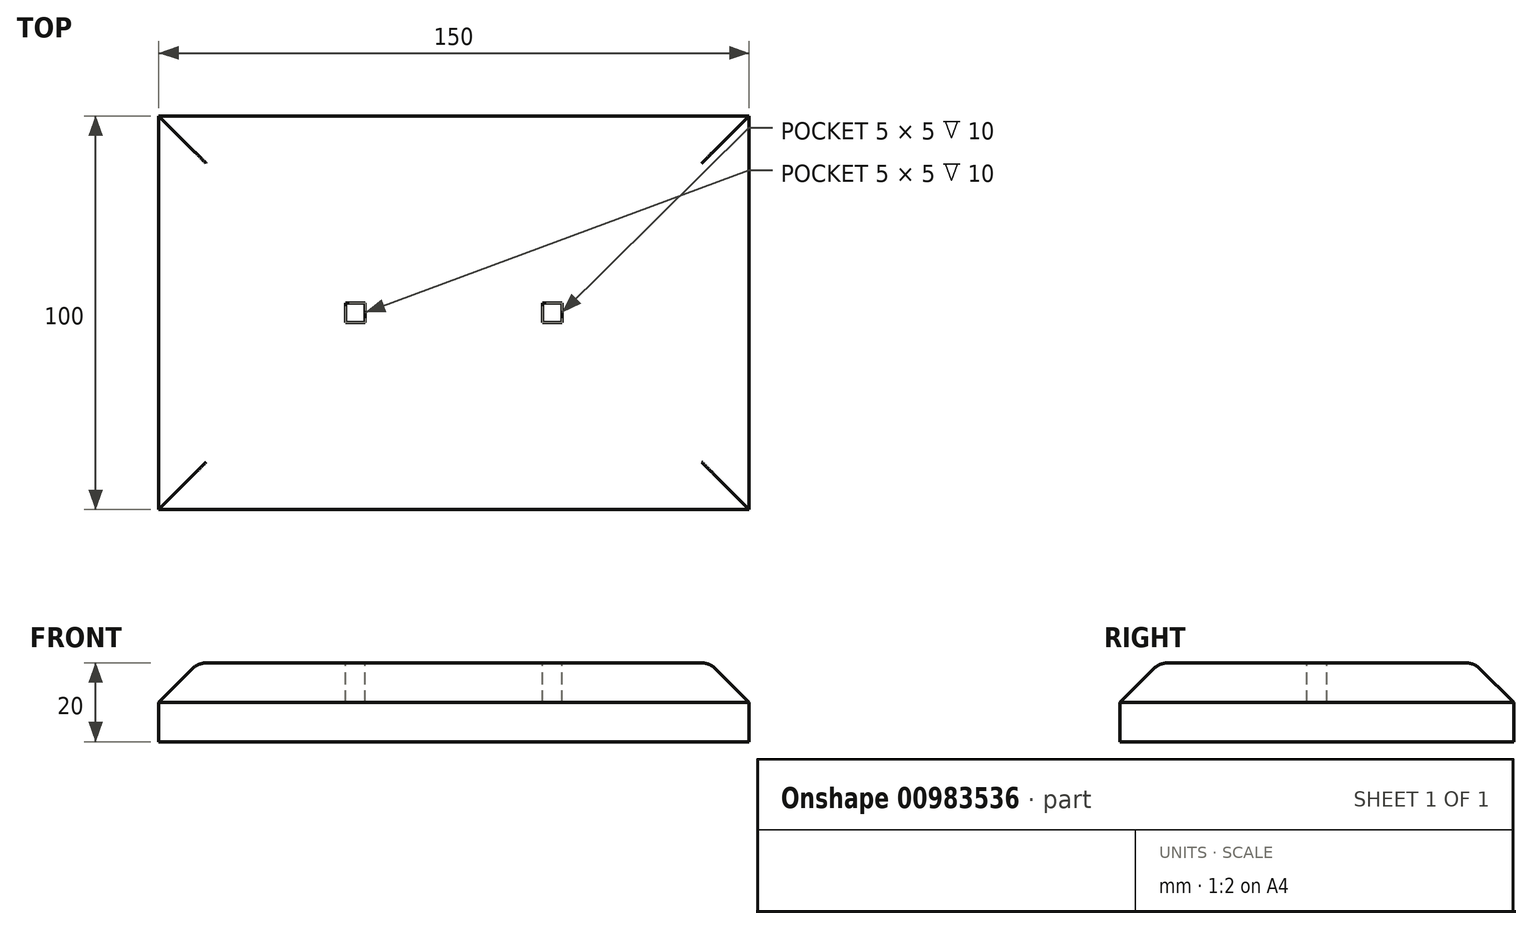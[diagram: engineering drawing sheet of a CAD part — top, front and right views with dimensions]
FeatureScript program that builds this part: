
annotation { "Feature Type Name" : "Feature", "Feature Type Description" : "" }
export const myFeature = defineFeature(function(context is Context, id is Id, definition is map)
    precondition{}
    {
        {
            var Q0;
            Q0=qCreatedBy(makeId("Top.planeOp"),FACE);
            var sketch = newSketch(context, id + "F0", { "sketchPlane" : qUnion([Q0])});
            skLineSegment(sketch, "E0.bottom", {"start": v(-65.87, 0) * mm, "end": v(84.13, 0) * mm});
            skLineSegment(sketch, "E0.top", {"start": v(-65.87, -100) * mm, "end": v(84.13, -100) * mm});
            skLineSegment(sketch, "E0.left", {"start": v(-65.87, 0) * mm, "end": v(-65.87, -100) * mm});
            skLineSegment(sketch, "E0.right", {"start": v(84.13, 0) * mm, "end": v(84.13, -100) * mm});
            skSolve(sketch);
        }
        {
            var Q0;
            Q0 = qSketchRegion(id + "F0", true);
            extrude(context, id + "F1", {"entities" : qUnion([Q0]), "depth" : 20 * mm, "offsetDistance" : 25 * mm});
        }
        {
            var Q0;
            Q0=makeQuery(id+"F1.opExtrude","CAP_EDGE",EDGE,{"disambiguationData":[OSD([sQuery(id+"F0.wireOp",EDGE,"E0.top")])],"isStart":false});
            var Q1;
            Q1=makeQuery(id+"F1.opExtrude","CAP_EDGE",EDGE,{"disambiguationData":[OSD([sQuery(id+"F0.wireOp",EDGE,"E0.left")])],"isStart":false});
            var Q2;
            Q2=makeQuery(id+"F1.opExtrude","CAP_EDGE",EDGE,{"disambiguationData":[OSD([sQuery(id+"F0.wireOp",EDGE,"E0.bottom")])],"isStart":false});
            var Q3;
            Q3=makeQuery(id+"F1.opExtrude","CAP_EDGE",EDGE,{"disambiguationData":[OSD([sQuery(id+"F0.wireOp",EDGE,"E0.right")])],"isStart":false});
            chamfer(context, id + "F2", {"entities" : qUnion([Q0, Q1, Q2, Q3]), "width" : 10 * mm, "tangentPropagation" : true});
        }
        {
            var Q0;
            Q0=makeQuery(id+"F1.opExtrude","CAP_FACE",FACE,{"disambiguationData":[OSD([sQuery(id+"F0.wireOp",EDGE,"E0.bottom"),sQuery(id+"F0.wireOp",EDGE,"E0.top"),sQuery(id+"F0.wireOp",EDGE,"E0.left"),sQuery(id+"F0.wireOp",EDGE,"E0.right")])],"isStart":false});
            var sketch = newSketch(context, id + "F3", { "sketchPlane" : qUnion([Q0])});
            skLineSegment(sketch, "E1", {"start": v(-55.87, -50) * mm, "end": v(74.13, -50) * mm});
            skLineSegment(sketch, "E2", {"start": v(9.13, -90) * mm, "end": v(9.13, -10) * mm});
            skLineSegment(sketch, "E3", {"start": v(9.13, -50) * mm, "end": v(34.13, -50) * mm});
            skLineSegment(sketch, "E4", {"start": v(34.13, -50) * mm, "end": v(34.13, -47.5) * mm});
            skLineSegment(sketch, "E5", {"start": v(31.63, -47.5) * mm, "end": v(34.13, -47.5) * mm});
            skLineSegment(sketch, "E6", {"start": v(31.63, -47.5) * mm, "end": v(31.63, -52.5) * mm});
            skLineSegment(sketch, "E7", {"start": v(31.63, -52.5) * mm, "end": v(36.63, -52.5) * mm});
            skLineSegment(sketch, "E8", {"start": v(36.63, -47.5) * mm, "end": v(36.63, -52.5) * mm});
            skLineSegment(sketch, "E9", {"start": v(36.63, -47.5) * mm, "end": v(34.13, -47.5) * mm});
            skLineSegment(sketch, "E10", {"start": v(9.13, -50) * mm, "end": v(-15.87, -50) * mm});
            skLineSegment(sketch, "E11", {"start": v(-15.87, -47.5) * mm, "end": v(-13.37, -47.5) * mm});
            skLineSegment(sketch, "E12", {"start": v(-13.37, -47.5) * mm, "end": v(-13.37, -52.5) * mm});
            skLineSegment(sketch, "E13", {"start": v(-13.37, -52.5) * mm, "end": v(-18.37, -52.5) * mm});
            skLineSegment(sketch, "E14", {"start": v(-18.37, -52.5) * mm, "end": v(-18.37, -47.5) * mm});
            skLineSegment(sketch, "E15", {"start": v(-18.37, -47.5) * mm, "end": v(-13.37, -47.5) * mm});
            skSolve(sketch);
        }
        {
            var Q0;
            Q0 = qSketchRegion(id + "F3", true);
            extrude(context, id + "F4", {"entities" : qUnion([Q0]), "operationType" : NewBodyOperationType.REMOVE, "oppositeDirection" : true, "depth" : 10 * mm, "offsetDistance" : 25 * mm});
        }
        {
            var Q0;
            {var subQ0=sQuery(id+"F0.wireOp",EDGE,"E0.top");Q0=makeQuery(id+"F2.opChamfer","BLEND_EDGE",EDGE,{"blendedFrom":[makeQuery(id+"F1.opExtrude","CAP_EDGE",EDGE,{"disambiguationData":[OSD([subQ0])],"isStart":false}),makeQuery(id+"F1.opExtrude","CAP_FACE",FACE,{"disambiguationData":[OSD([sQuery(id+"F0.wireOp",EDGE,"E0.bottom"),subQ0,sQuery(id+"F0.wireOp",EDGE,"E0.left"),sQuery(id+"F0.wireOp",EDGE,"E0.right")])],"isStart":false})],"blendedInto":[makeQuery(id+"F1.opExtrude","CAP_FACE",FACE,{"disambiguationData":[OSD([sQuery(id+"F0.wireOp",EDGE,"E0.bottom"),subQ0,sQuery(id+"F0.wireOp",EDGE,"E0.left"),sQuery(id+"F0.wireOp",EDGE,"E0.right")])],"isStart":false})]});}
            var Q1;
            {var subQ0=sQuery(id+"F0.wireOp",EDGE,"E0.left");Q1=makeQuery(id+"F2.opChamfer","BLEND_EDGE",EDGE,{"blendedFrom":[makeQuery(id+"F1.opExtrude","CAP_EDGE",EDGE,{"disambiguationData":[OSD([subQ0])],"isStart":false}),makeQuery(id+"F1.opExtrude","CAP_FACE",FACE,{"disambiguationData":[OSD([sQuery(id+"F0.wireOp",EDGE,"E0.bottom"),sQuery(id+"F0.wireOp",EDGE,"E0.top"),subQ0,sQuery(id+"F0.wireOp",EDGE,"E0.right")])],"isStart":false})],"blendedInto":[makeQuery(id+"F1.opExtrude","CAP_FACE",FACE,{"disambiguationData":[OSD([sQuery(id+"F0.wireOp",EDGE,"E0.bottom"),sQuery(id+"F0.wireOp",EDGE,"E0.top"),subQ0,sQuery(id+"F0.wireOp",EDGE,"E0.right")])],"isStart":false})]});}
            var Q2;
            {var subQ0=sQuery(id+"F0.wireOp",EDGE,"E0.right");Q2=makeQuery(id+"F2.opChamfer","BLEND_EDGE",EDGE,{"blendedFrom":[makeQuery(id+"F1.opExtrude","CAP_EDGE",EDGE,{"disambiguationData":[OSD([subQ0])],"isStart":false}),makeQuery(id+"F1.opExtrude","CAP_FACE",FACE,{"disambiguationData":[OSD([sQuery(id+"F0.wireOp",EDGE,"E0.bottom"),sQuery(id+"F0.wireOp",EDGE,"E0.top"),sQuery(id+"F0.wireOp",EDGE,"E0.left"),subQ0])],"isStart":false})],"blendedInto":[makeQuery(id+"F1.opExtrude","CAP_FACE",FACE,{"disambiguationData":[OSD([sQuery(id+"F0.wireOp",EDGE,"E0.bottom"),sQuery(id+"F0.wireOp",EDGE,"E0.top"),sQuery(id+"F0.wireOp",EDGE,"E0.left"),subQ0])],"isStart":false})]});}
            var Q3;
            {var subQ0=sQuery(id+"F0.wireOp",EDGE,"E0.bottom");Q3=makeQuery(id+"F2.opChamfer","BLEND_EDGE",EDGE,{"blendedFrom":[makeQuery(id+"F1.opExtrude","CAP_EDGE",EDGE,{"disambiguationData":[OSD([subQ0])],"isStart":false}),makeQuery(id+"F1.opExtrude","CAP_FACE",FACE,{"disambiguationData":[OSD([subQ0,sQuery(id+"F0.wireOp",EDGE,"E0.top"),sQuery(id+"F0.wireOp",EDGE,"E0.left"),sQuery(id+"F0.wireOp",EDGE,"E0.right")])],"isStart":false})],"blendedInto":[makeQuery(id+"F1.opExtrude","CAP_FACE",FACE,{"disambiguationData":[OSD([subQ0,sQuery(id+"F0.wireOp",EDGE,"E0.top"),sQuery(id+"F0.wireOp",EDGE,"E0.left"),sQuery(id+"F0.wireOp",EDGE,"E0.right")])],"isStart":false})]});}
            fillet(context, id + "F5", {"entities" : qUnion([Q0, Q1, Q2, Q3]), "radius" : 5 * mm, "tangentPropagation" : true, "allowEdgeOverflow" : false});
        }
    });
